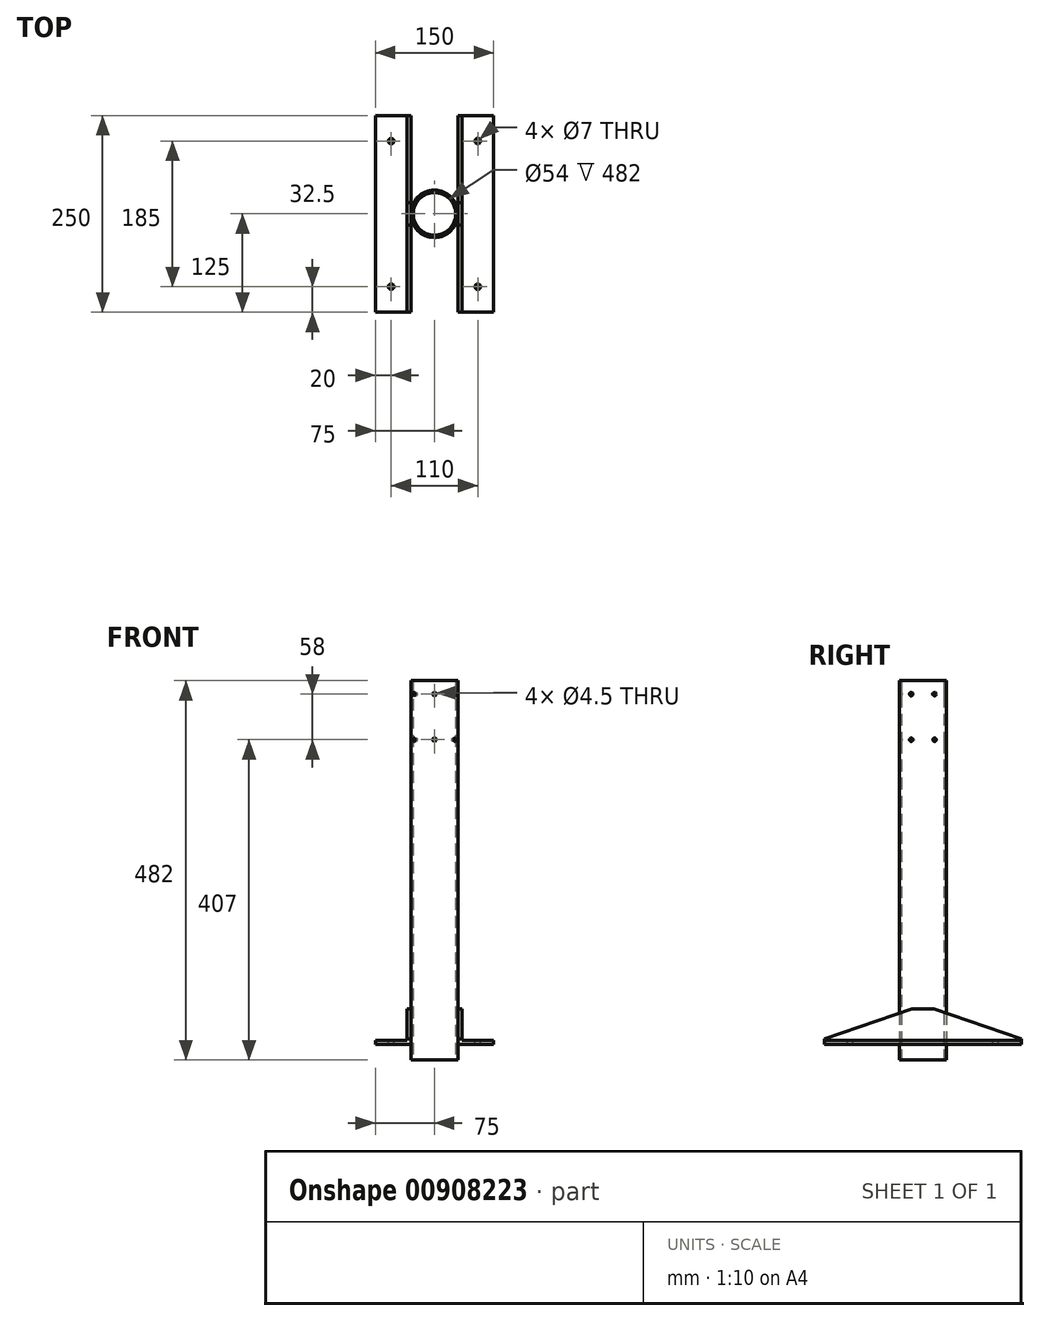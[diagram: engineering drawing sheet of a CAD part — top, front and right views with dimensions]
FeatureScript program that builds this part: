
annotation { "Feature Type Name" : "Feature", "Feature Type Description" : "" }
export const myFeature = defineFeature(function(context is Context, id is Id, definition is map)
    precondition{}
    {
        {
            var Q0;
            Q0=qCreatedBy(makeId("Top.planeOp"),FACE);
            var sketch = newSketch(context, id + "F0", { "sketchPlane" : qUnion([Q0])});
            skCircle(sketch, "E0", {"center": v(0, 0) * mm, "radius": 30 * mm});
            skCircle(sketch, "E1", {"center": v(0, 0) * mm, "radius": 27 * mm});
            skSolve(sketch);
        }
        {
            var Q0;
            Q0 = qSketchRegion(id + "F0", true);
            extrude(context, id + "F1", {"entities" : qUnion([Q0]), "depth" : 482 * mm, "offsetDistance" : 25 * mm});
        }
        {
            var Q0;
            Q0=qCreatedBy(makeId("Front.planeOp"),FACE);
            var sketch = newSketch(context, id + "F2", { "sketchPlane" : qUnion([Q0])});
            skLineSegment(sketch, "E2", {"start": v(-30, 65) * mm, "end": v(-30, 20) * mm});
            skLineSegment(sketch, "E3", {"start": v(-30, 20) * mm, "end": v(-75, 20) * mm});
            skLineSegment(sketch, "E4", {"start": v(-75, 20) * mm, "end": v(-75, 25) * mm});
            skLineSegment(sketch, "E5", {"start": v(-75, 25) * mm, "end": v(-35, 25) * mm});
            skLineSegment(sketch, "E6", {"start": v(-35, 25) * mm, "end": v(-35, 65) * mm});
            skLineSegment(sketch, "E7", {"start": v(-35, 65) * mm, "end": v(-30, 65) * mm});
            skLineSegment(sketch, "E8", {"start": v(-30, 0) * mm, "end": v(-30, 20) * mm, "construction": true});
            skSolve(sketch);
        }
        {
            var Q0;
            Q0=makeQuery(id+"F2.imprint","IMPRINT",FACE,{"disambiguationData":[TD([[makeQuery(id+"F2.imprint","IMPRINT",EDGE,{"derivedFrom":sQuery(id+"F2.wireOp",EDGE,"E2")}),-1.0]])]});
            extrude(context, id + "F3", {"entities" : qUnion([Q0]), "depth" : 250 * mm, "offsetDistance" : 25 * mm, "symmetric" : true});
        }
        {
            var Q0;
            Q0=makeQuery(id+"F3.opExtrude","SWEPT_FACE",FACE,{"disambiguationData":[OSD([sQuery(id+"F2.wireOp",EDGE,"E6")])]});
            var sketch = newSketch(context, id + "F4", { "sketchPlane" : qUnion([Q0])});
            skLineSegment(sketch, "E9", {"start": v(-125, 25) * mm, "end": v(-125, 27) * mm, "construction": true});
            skLineSegment(sketch, "E10", {"start": v(-125, 27) * mm, "end": v(-14, 65) * mm});
            skLineSegment(sketch, "E11", {"start": v(-14, 65) * mm, "end": v(-125, 65) * mm});
            skLineSegment(sketch, "E12", {"start": v(-125, 65) * mm, "end": v(-125, 27) * mm});
            skSolve(sketch);
        }
        {
            var Q0;
            Q0 = qSketchRegion(id + "F4", true);
            extrude(context, id + "F5", {"entities" : qUnion([Q0]), "endBound" : BoundingType.UP_TO_NEXT, "oppositeDirection" : true, "depth" : 25 * mm, "offsetDistance" : 25 * mm});
        }
        {
            var Q0;
            Q0=makeQuery(id+"F5.opExtrude","SWEPT_BODY",BODY,{"disambiguationData":[OSD([sQuery(id+"F4.wireOp",EDGE,"E10"),sQuery(id+"F4.wireOp",EDGE,"E11"),sQuery(id+"F4.wireOp",EDGE,"E12")])]});
            var Q1;
            Q1=qCreatedBy(makeId("Front.planeOp"),FACE);
            mirror(context, id + "F6", {"operationType" : NewBodyOperationType.REMOVE, "entities" : qUnion([Q0]), "mirrorPlane" : qUnion([Q1])});
        }
        {
            var Q0;
            Q0=makeQuery(id+"F5.opExtrude","SWEPT_BODY",BODY,{"disambiguationData":[OSD([sQuery(id+"F4.wireOp",EDGE,"E10"),sQuery(id+"F4.wireOp",EDGE,"E11"),sQuery(id+"F4.wireOp",EDGE,"E12")])]});
            var Q1;
            Q1=makeQuery(id+"F3.opExtrude","SWEPT_BODY",BODY,{"disambiguationData":[OSD([sQuery(id+"F2.wireOp",EDGE,"E2"),sQuery(id+"F2.wireOp",EDGE,"E3"),sQuery(id+"F2.wireOp",EDGE,"E4"),sQuery(id+"F2.wireOp",EDGE,"E5"),sQuery(id+"F2.wireOp",EDGE,"E6"),sQuery(id+"F2.wireOp",EDGE,"E7")])]});
            booleanBodies(context, id + "F7", {"operationType" : BooleanOperationType.SUBTRACTION, "tools" : qUnion([Q0]), "targets" : qUnion([Q1])});
        }
        {
            var Q0;
            Q0=makeQuery(id+"F3.opExtrude","SWEPT_BODY",BODY,{"disambiguationData":[OSD([sQuery(id+"F2.wireOp",EDGE,"E2"),sQuery(id+"F2.wireOp",EDGE,"E3"),sQuery(id+"F2.wireOp",EDGE,"E4"),sQuery(id+"F2.wireOp",EDGE,"E5"),sQuery(id+"F2.wireOp",EDGE,"E6"),sQuery(id+"F2.wireOp",EDGE,"E7")])]});
            var Q1;
            Q1=qCreatedBy(makeId("Right.planeOp"),FACE);
            mirror(context, id + "F8", {"entities" : qUnion([Q0]), "mirrorPlane" : qUnion([Q1])});
        }
        {
            var Q0;
            Q0=makeQuery(id+"F8.opPattern","COPY",FACE,{"derivedFrom":makeQuery(id+"F3.opExtrude","SWEPT_FACE",FACE,{"disambiguationData":[OSD([sQuery(id+"F2.wireOp",EDGE,"E5")])]}),"instanceName":"1"});
            var sketch = newSketch(context, id + "F9", { "sketchPlane" : qUnion([Q0])});
            skCircle(sketch, "E13", {"center": v(-55, 92.5) * mm, "radius": 3.5 * mm});
            skCircle(sketch, "E14", {"center": v(-55, -92.5) * mm, "radius": 3.5 * mm});
            skCircle(sketch, "E15", {"center": v(55, 92.5) * mm, "radius": 3.5 * mm});
            skCircle(sketch, "E16", {"center": v(55, -92.5) * mm, "radius": 3.5 * mm});
            skLineSegment(sketch, "E17", {"start": v(0, 0) * mm, "end": v(-125.64, 0) * mm, "construction": true});
            skLineSegment(sketch, "E18", {"start": v(0, 0) * mm, "end": v(0, 103.02) * mm, "construction": true});
            skSolve(sketch);
        }
        {
            var Q0;
            Q0 = qSketchRegion(id + "F9", true);
            extrude(context, id + "F10", {"entities" : qUnion([Q0]), "operationType" : NewBodyOperationType.REMOVE, "endBound" : BoundingType.UP_TO_NEXT, "oppositeDirection" : true, "depth" : 25 * mm, "offsetDistance" : 25 * mm});
        }
        {
            var Q0;
            Q0=qCreatedBy(makeId("Front.planeOp"),FACE);
            var sketch = newSketch(context, id + "F11", { "sketchPlane" : qUnion([Q0])});
            skCircle(sketch, "E19", {"center": v(0, 465) * mm, "radius": 2.25 * mm});
            skCircle(sketch, "E20", {"center": v(0, 407) * mm, "radius": 2.25 * mm});
            skSolve(sketch);
        }
        {
            var Q0;
            Q0 = qSketchRegion(id + "F11", true);
            var Q1;
            Q1=makeQuery(id+"F1.opExtrude","SWEPT_FACE",FACE,{"disambiguationData":[OSD([sQuery(id+"F0.wireOp",EDGE,"E0")])]});
            extrude(context, id + "F12", {"entities" : qUnion([Q0]), "endBound" : BoundingType.UP_TO_SURFACE, "depth" : 25 * mm, "endBoundEntityFace" : qUnion([Q1]), "offsetDistance" : 25 * mm});
        }
        {
            var Q0;
            Q0=makeQuery(id+"F12.opExtrude","SWEPT_BODY",BODY,{"disambiguationData":[OSD([sQuery(id+"F11.wireOp",EDGE,"E19")])]});
            var Q1;
            Q1=makeQuery(id+"F12.opExtrude","SWEPT_BODY",BODY,{"disambiguationData":[OSD([sQuery(id+"F11.wireOp",EDGE,"E20")])]});
            var Q2;
            Q2=makeQuery(id+"F1.opExtrude","SWEPT_FACE",FACE,{"disambiguationData":[OSD([sQuery(id+"F0.wireOp",EDGE,"E1")])]});
            circularPattern(context, id + "F13", {"operationType" : NewBodyOperationType.REMOVE, "entities" : qUnion([Q0, Q1]), "axis" : qUnion([Q2]), "angle" : 360 * degree, "instanceCount" : 6, "equalSpace" : true});
        }
    });
